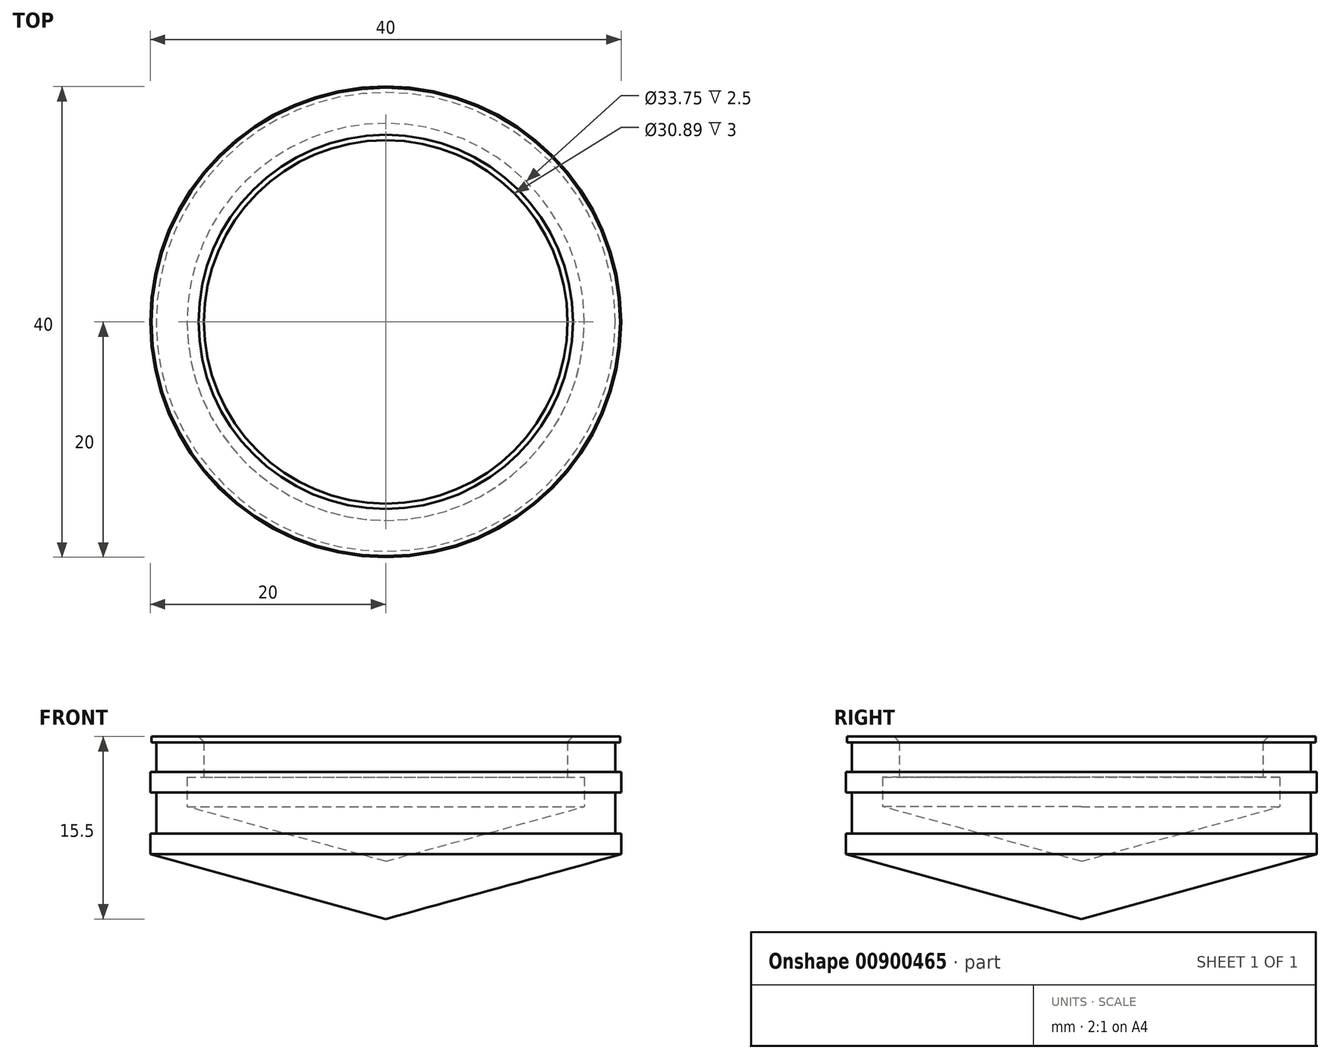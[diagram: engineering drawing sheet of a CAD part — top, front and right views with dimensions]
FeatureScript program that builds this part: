
annotation { "Feature Type Name" : "Feature", "Feature Type Description" : "" }
export const myFeature = defineFeature(function(context is Context, id is Id, definition is map)
    precondition{}
    {
        {
            var Q0;
            Q0=qCreatedBy(makeId("Front.planeOp"),FACE);
            var sketch = newSketch(context, id + "F0", { "sketchPlane" : qUnion([Q0])});
            skLineSegment(sketch, "E0", {"start": v(-19.9, 0) * mm, "end": v(-19.9, -0.5) * mm});
            skLineSegment(sketch, "E1", {"start": v(-19.9, -0.5) * mm, "end": v(-19.5, -0.5) * mm});
            skLineSegment(sketch, "E2", {"start": v(-19.5, -0.5) * mm, "end": v(-19.5, -3) * mm});
            skLineSegment(sketch, "E3", {"start": v(-19.5, -3) * mm, "end": v(-20, -3) * mm});
            skLineSegment(sketch, "E4", {"start": v(-20, -3) * mm, "end": v(-20, -4.75) * mm});
            skLineSegment(sketch, "E5", {"start": v(-20, -4.75) * mm, "end": v(-19.5, -4.75) * mm});
            skLineSegment(sketch, "E6", {"start": v(-19.5, -4.75) * mm, "end": v(-19.5, -8.25) * mm});
            skLineSegment(sketch, "E7", {"start": v(-19.5, -8.25) * mm, "end": v(-20, -8.25) * mm});
            skLineSegment(sketch, "E8", {"start": v(-20, -8.25) * mm, "end": v(-20, -10) * mm});
            skLineSegment(sketch, "E9", {"start": v(-20, -10) * mm, "end": v(0, -15.5) * mm});
            skLineSegment(sketch, "E10", {"start": v(0, -15.5) * mm, "end": v(0, -10.6) * mm});
            skLineSegment(sketch, "E11", {"start": v(0, -10.6) * mm, "end": v(-16.88, -5.95) * mm});
            skLineSegment(sketch, "E12", {"start": v(-16.88, -5.95) * mm, "end": v(-16.88, -3.45) * mm});
            skLineSegment(sketch, "E13", {"start": v(-16.88, -3.45) * mm, "end": v(-15.45, -3.45) * mm});
            skLineSegment(sketch, "E14", {"start": v(-15.45, -3.45) * mm, "end": v(-15.45, -0.45) * mm});
            skLineSegment(sketch, "E15", {"start": v(-15.45, -0.45) * mm, "end": v(-15.9, 0) * mm});
            skLineSegment(sketch, "E16", {"start": v(-15.9, 0) * mm, "end": v(-19.9, 0) * mm});
            skSolve(sketch);
        }
        {
            var Q0;
            Q0 = qSketchRegion(id + "F0", true);
            var Q1;
            Q1=sQuery(id+"F0.wireOp",EDGE,"E10");
            revolve(context, id + "F1", {"surfaceOperationType" : NewSurfaceOperationType.NEW, "entities" : qUnion([Q0]), "axis" : qUnion([Q1]), "revolveType" : RevolveType.FULL});
        }
    });
